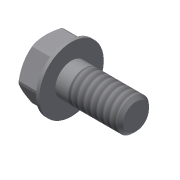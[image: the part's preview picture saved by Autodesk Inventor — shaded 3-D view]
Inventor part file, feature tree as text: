
AUTODESK INVENTOR PART (.ipt)
format: ipt  version: 2022.5 (Build 265521000, 521)  size: 126,464 bytes
history: native  units: in
note: dims shown in document units (in); Inventor stores cm internally (conversion verified against a paired STEP export)
features: sketch x2, revolve x1, chamfer x1, extrude x1, thread x1
ambient origin geometry x8: Origin, YZ Plane, XZ Plane, XY Plane, X Axis, Y Axis, Z Axis, Center Point
bodies: Solid1 (feature_tree)
feature tree (6):
  revolve  "Revolution1"  [1 undecoded]
  chamfer  "Chamfer4"  Distance=0.0157in
  extrude  "Extrusion15"  Depth=0.126in
  thread  "Thread3"  [1 undecoded]
  sketch  "Sketch15"  dims[d21=0.7874in d78=0.0079in]
  sketch  "Sketch16"  dims[d84=0.0394in d86=0.0157in d87=0.0709in d89=0.0591in d90=0.0787in d92=90.0deg d97=0.0079in d98=0.0787in d99=45.0deg d104=0.126in d105=0.3937in d106=0.0in d111=0.1575in d112=0.1181in d113=0.0in]
note: 2 required parameter values undecoded (feature->parameter linkage not recoverable at this tier; creation-order binding heuristic only, values carry confidence <= 0.55)